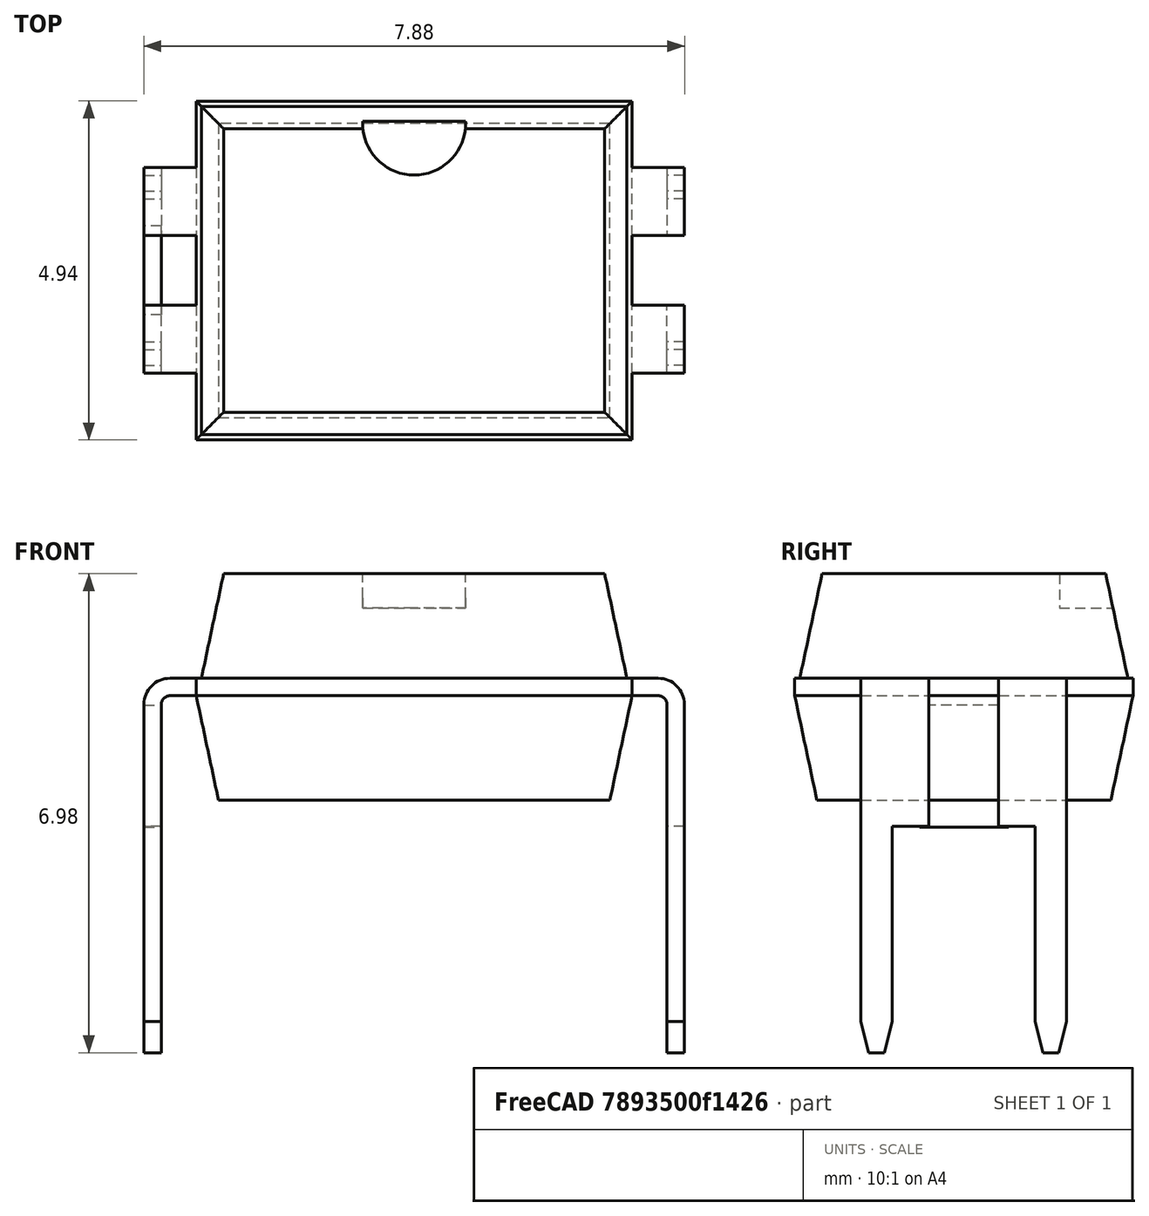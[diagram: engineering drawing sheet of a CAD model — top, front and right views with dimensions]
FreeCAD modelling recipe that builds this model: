
FCSTD DOCUMENT  (FreeCAD 0.16R6712 (Git))
Label: Vishay_HVM-DIP-3_W7.62mm
License: All rights reserved
LicenseURL: http://en.wikipedia.org/wiki/All_rights_reserved
objects: Part::Feature×1, Sketcher::SketchObject×1, PartDesign::Pad×1, Part::MultiFuse×1
note: 5 computed .brp shape members not serialized (recipe doc carries the construction recipe); baked Part::Feature solids carry a one-line shape summary decoded from their .brp

FEATURE [Part::Feature] Part__Feature  label="DIP-4"
  shape: bbox 7.874 x 4.93 x 6.98 mm, 80 faces (baked)
FEATURE [Sketcher::SketchObject] Sketch001
  Placement = pos=(0,0,0) rot=(0.57735,0.57735,0.57735;2.0944rad)
  sketch-geometry (4):
    g0: LineSegment StartX=-1.91341 StartY=-0.012161 StartZ=0 EndX=-0.620514 EndY=-0.012161 EndZ=0
    g1: LineSegment StartX=-0.620514 StartY=-0.012161 StartZ=0 EndX=-0.620514 EndY=1.76433 EndZ=0
    g2: LineSegment StartX=-0.620514 StartY=1.76433 StartZ=0 EndX=-1.91341 EndY=1.76433 EndZ=0
    g3: LineSegment StartX=-1.91341 StartY=1.76433 StartZ=0 EndX=-1.91341 EndY=-0.012161 EndZ=0
  constraints (8):
    c: Coincident(g0,g1)
    c: Coincident(g1,g2)
    c: Coincident(g2,g3)
    c: Coincident(g3,g0)
    c: Horizontal(g0)
    c: Horizontal(g2)
    c: Vertical(g1)
    c: Vertical(g3)
FEATURE [PartDesign::Pad] Pad001
  Length = 0.25
  Length2 = 100
  Midplane = true
  Placement = pos=(0,0,0) rot=(0.57735,0.57735,0.57735;2.0944rad)
  Sketch = -> Sketch001
  Type = 0
FEATURE [Part::MultiFuse] Vishay_HVM_DIP_3_W7_62mm_mp_cp  label="Vishay_HVM-DIP-3_W7.62mm"
  Shapes = -> [Part__Feature,Pad001]
